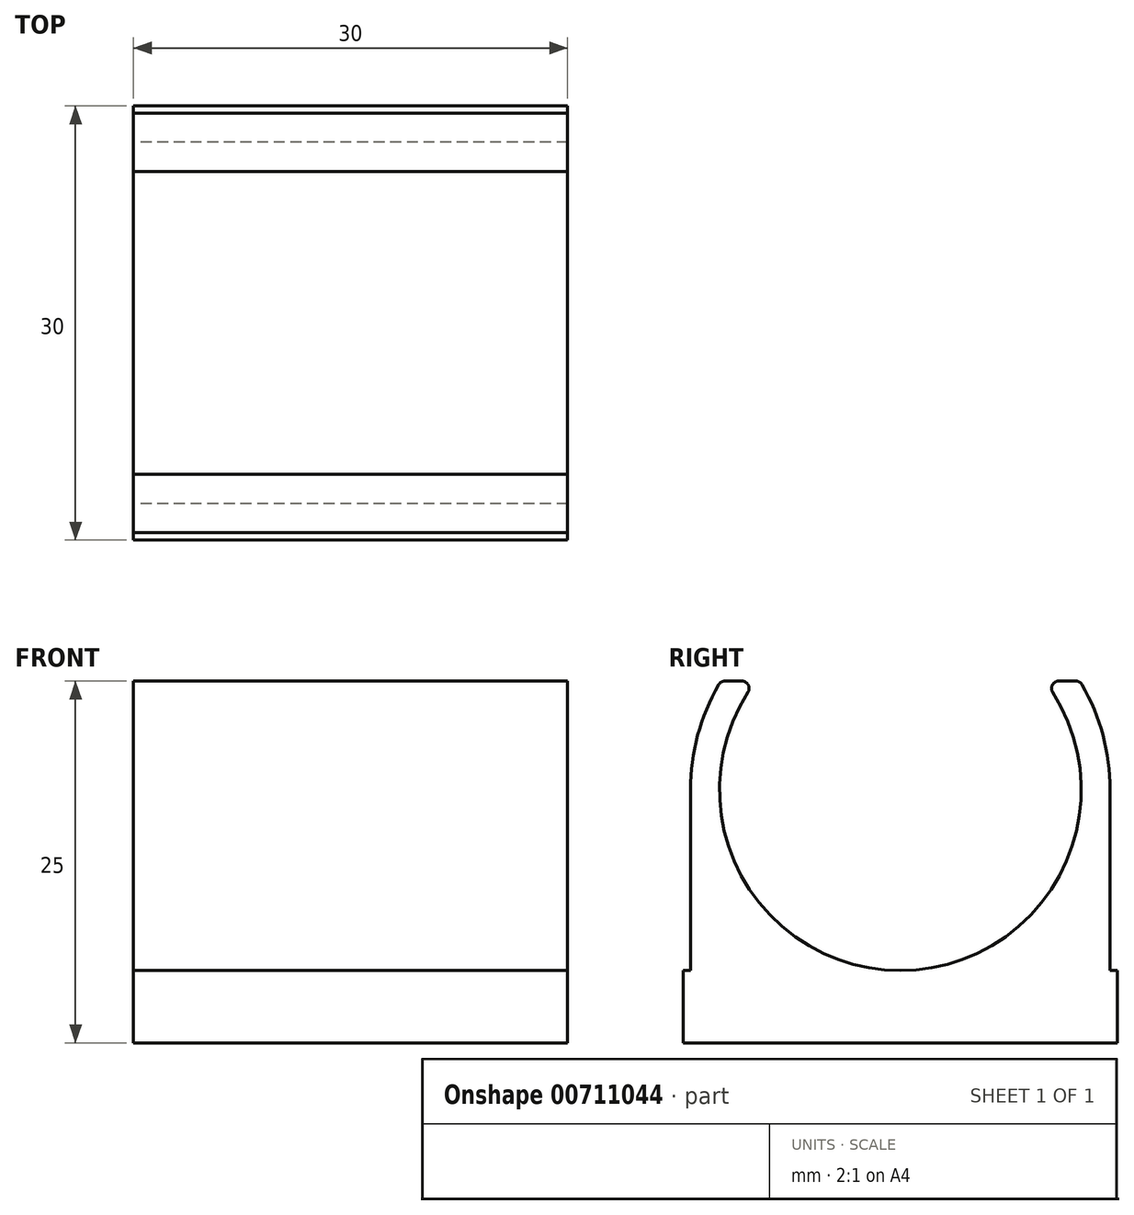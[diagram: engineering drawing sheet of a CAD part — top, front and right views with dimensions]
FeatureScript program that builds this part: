
annotation { "Feature Type Name" : "Feature", "Feature Type Description" : "" }
export const myFeature = defineFeature(function(context is Context, id is Id, definition is map)
    precondition{}
    {
        {
            var Q0;
            Q0=qCreatedBy(makeId("Top.planeOp"),FACE);
            var sketch = newSketch(context, id + "F0", { "sketchPlane" : qUnion([Q0])});
            skLineSegment(sketch, "E0.bottom", {"start": v(15, 15) * mm, "end": v(-15, 15) * mm});
            skLineSegment(sketch, "E0.top", {"start": v(15, -15) * mm, "end": v(-15, -15) * mm});
            skLineSegment(sketch, "E0.left", {"start": v(15, 15) * mm, "end": v(15, -15) * mm});
            skLineSegment(sketch, "E0.right", {"start": v(-15, 15) * mm, "end": v(-15, -15) * mm});
            skPoint(sketch, "E0.middle", {"position": v(0, 0) * mm});
            skSolve(sketch);
        }
        {
            var Q0;
            Q0=makeQuery(id+"F0.imprint","IMPRINT",FACE,{"disambiguationData":[TD([[makeQuery(id+"F0.imprint","IMPRINT",EDGE,{"derivedFrom":sQuery(id+"F0.wireOp",EDGE,"E0.bottom")}),1.0]])]});
            extrude(context, id + "F1", {"entities" : qUnion([Q0]), "oppositeDirection" : true, "depth" : 5 * mm, "offsetDistance" : 25 * mm});
        }
        {
            var Q0;
            Q0=makeQuery(id+"F1.opExtrude","SWEPT_FACE",FACE,{"disambiguationData":[OSD([sQuery(id+"F0.wireOp",EDGE,"E0.right")])]});
            var sketch = newSketch(context, id + "F2", { "sketchPlane" : qUnion([Q0])});
            skArc(sketch, "E1", {"start": v(-10, 20) * mm, "mid": v(0, 0) * mm, "end": v(10, 20) * mm});
            skArc(sketch, "E2", {"start": v(-12.4, 20) * mm, "mid": v(-13.97, 16.4) * mm, "end": v(-14.5, 12.5) * mm});
            skLineSegment(sketch, "E3", {"start": v(-14.5, 12.5) * mm, "end": v(-14.5, 0) * mm});
            skLineSegment(sketch, "E4", {"start": v(14.5, 12.5) * mm, "end": v(14.5, 0) * mm});
            skLineSegment(sketch, "E5", {"start": v(-12.4, 20) * mm, "end": v(12.4, 20) * mm});
            skArc(sketch, "E6.trimOffspring", {"start": v(14.5, 12.5) * mm, "mid": v(13.97, 16.4) * mm, "end": v(12.4, 20) * mm});
            skSolve(sketch);
        }
        {
            var Q0;
            {var subQ4=sQuery(id+"F2.wireOp",EDGE,"E4");Q0=makeQuery(id+"F2.imprint","IMPRINT",FACE,{"disambiguationData":[TD([[makeQuery(id+"F2.imprint","IMPRINT",EDGE,{"derivedFrom":subQ4}),-1.0]])]});}
            var Q1;
            {var subQ4=sQuery(id+"F2.wireOp",EDGE,"E2");Q1=makeQuery(id+"F2.imprint","IMPRINT",FACE,{"disambiguationData":[TD([[makeQuery(id+"F2.imprint","IMPRINT",EDGE,{"derivedFrom":subQ4}),1.0]])]});}
            extrude(context, id + "F3", {"entities" : qUnion([Q0, Q1]), "operationType" : NewBodyOperationType.ADD, "oppositeDirection" : true, "depth" : 30 * mm, "offsetDistance" : 25 * mm});
        }
        {
            var Q0;
            {var subQ0=sQuery(id+"F2.wireOp",EDGE,"E5");var subQ1=sQuery(id+"F2.wireOp",EDGE,"E1");Q0=makeQuery(id+"F3.opExtrude","SWEPT_EDGE",EDGE,{"disambiguationData":[OSD([subQ1,subQ0]),TDD([makeQuery(id+"F2.imprint","INTERSECT",VERTEX,{"disambiguationData":[OD(1.0)],"derivedFrom":[subQ1,subQ0]})])]});}
            var Q1;
            {var subQ0=sQuery(id+"F2.wireOp",EDGE,"E5");var subQ1=sQuery(id+"F2.wireOp",EDGE,"E1");Q1=makeQuery(id+"F3.opExtrude","SWEPT_EDGE",EDGE,{"disambiguationData":[OSD([subQ1,subQ0]),TDD([makeQuery(id+"F2.imprint","INTERSECT",VERTEX,{"disambiguationData":[OD(0.0)],"derivedFrom":[subQ1,subQ0]})])]});}
            var Q2;
            Q2=makeQuery(id+"F3.opExtrude","SWEPT_EDGE",EDGE,{"disambiguationData":[OSD([sQuery(id+"F2.wireOp",EDGE,"E5"),sQuery(id+"F2.wireOp",EDGE,"E6.trimOffspring")])]});
            var Q3;
            Q3=makeQuery(id+"F3.opExtrude","SWEPT_EDGE",EDGE,{"disambiguationData":[OSD([sQuery(id+"F2.wireOp",EDGE,"E2"),sQuery(id+"F2.wireOp",EDGE,"E5")])]});
            fillet(context, id + "F4", {"entities" : qUnion([Q0, Q1, Q2, Q3]), "radius" : 0.5 * mm, "tangentPropagation" : true, "allowEdgeOverflow" : false});
        }
    });
